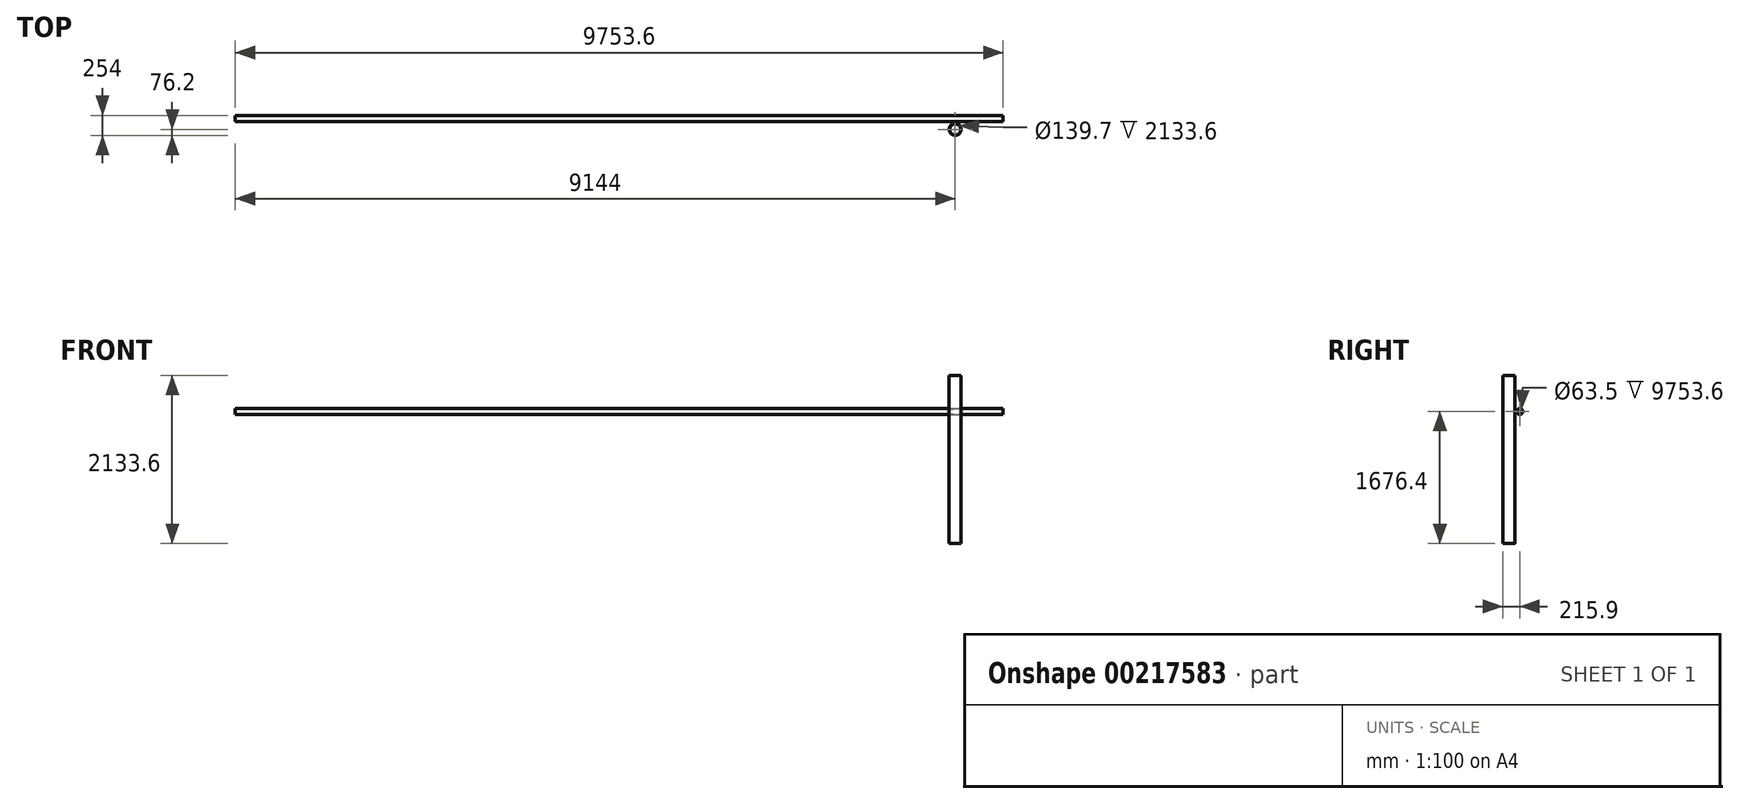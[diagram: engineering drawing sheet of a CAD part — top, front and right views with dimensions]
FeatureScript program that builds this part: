
annotation { "Feature Type Name" : "Feature", "Feature Type Description" : "" }
export const myFeature = defineFeature(function(context is Context, id is Id, definition is map)
    precondition{}
    {
        {
            var Q0;
            Q0=qCreatedBy(makeId("Top.planeOp"),FACE);
            var sketch = newSketch(context, id + "F0", { "sketchPlane" : qUnion([Q0])});
            skCircle(sketch, "E0", {"center": v(0, 0) * mm, "radius": 76.2 * mm});
            skCircle(sketch, "E1", {"center": v(0, 0) * mm, "radius": 69.85 * mm});
            skSolve(sketch);
        }
        {
            var Q0;
            Q0 = qSketchRegion(id + "F0", true);
            extrude(context, id + "F1", {"entities" : qUnion([Q0]), "depth" : 1219.2 * mm, "hasSecondDirection" : true, "secondDirectionOppositeDirection" : true, "secondDirectionDepth" : 914.4 * mm});
        }
        {
            var Q0;
            Q0=qCreatedBy(makeId("Right.planeOp"),FACE);
            var sketch = newSketch(context, id + "F2", { "sketchPlane" : qUnion([Q0])});
            skCircle(sketch, "E2", {"center": v(139.7, 762) * mm, "radius": 38.1 * mm});
            skCircle(sketch, "E3", {"center": v(139.7, 762) * mm, "radius": 31.75 * mm});
            skSolve(sketch);
        }
        {
            var Q0;
            Q0 = qSketchRegion(id + "F2", true);
            extrude(context, id + "F3", {"entities" : qUnion([Q0]), "oppositeDirection" : true, "depth" : 9144 * mm, "hasSecondDirection" : true, "secondDirectionOppositeDirection" : false, "secondDirectionDepth" : 609.6 * mm});
        }
    });
